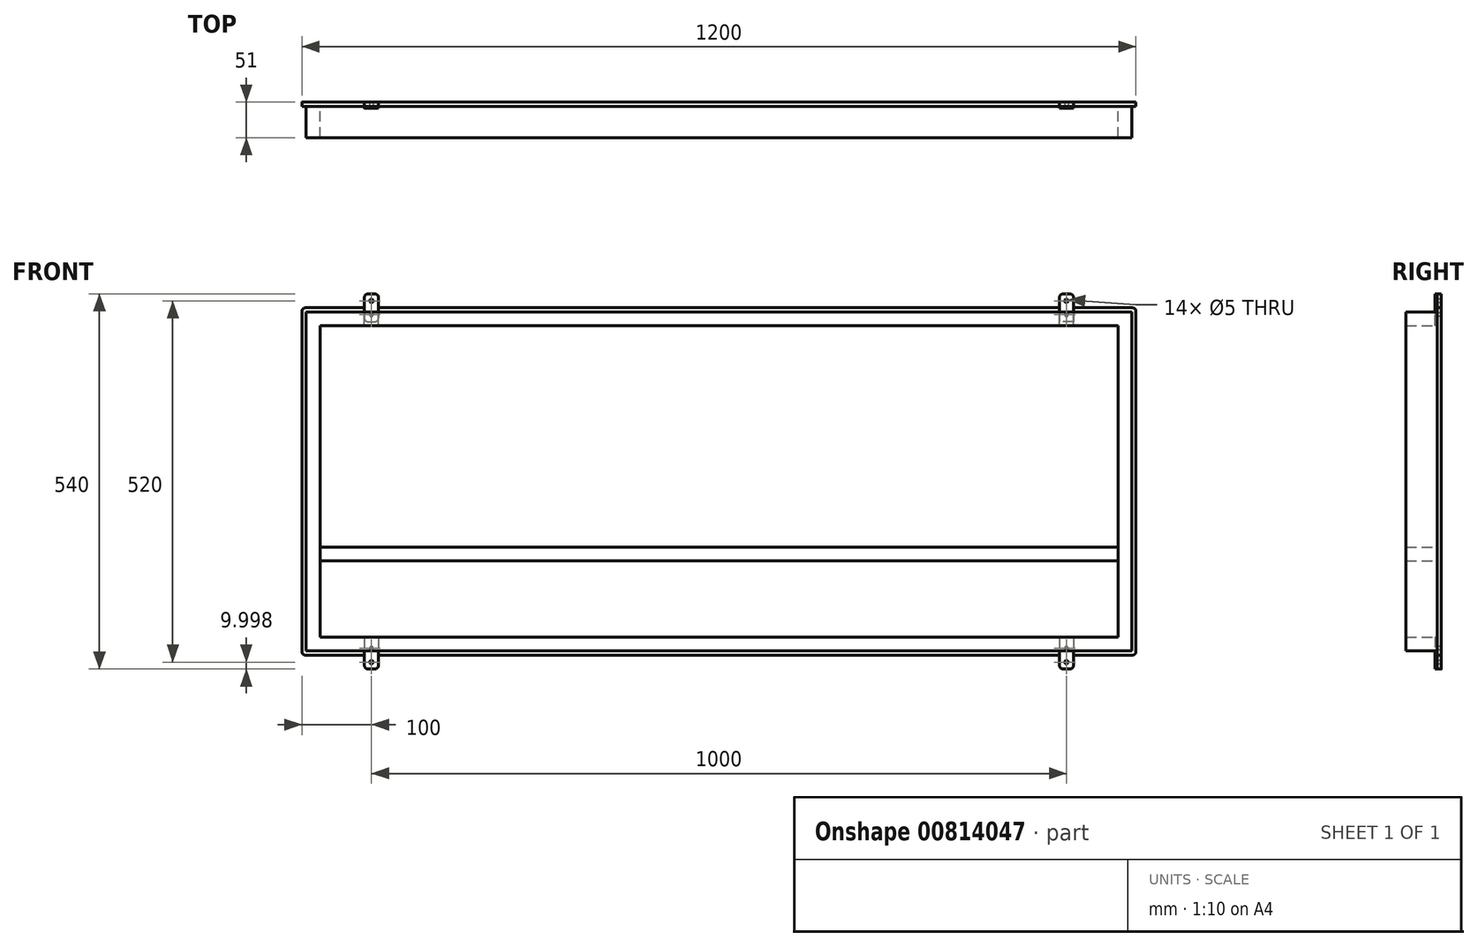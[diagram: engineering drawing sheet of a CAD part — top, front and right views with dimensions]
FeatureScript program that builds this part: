
annotation { "Feature Type Name" : "Feature", "Feature Type Description" : "" }
export const myFeature = defineFeature(function(context is Context, id is Id, definition is map)
    precondition{}
    {
        {
            var Q0;
            Q0=qCreatedBy(makeId("Front.planeOp"),FACE);
            var sketch = newSketch(context, id + "F0", { "sketchPlane" : qUnion([Q0])});
            skLineSegment(sketch, "E0.bottom", {"start": v(-594, 203.06) * mm, "end": v(594, 203.06) * mm});
            skLineSegment(sketch, "E0.top", {"start": v(-594, 223.06) * mm, "end": v(594, 223.06) * mm});
            skLineSegment(sketch, "E0.left", {"start": v(-594, 203.06) * mm, "end": v(-594, 223.06) * mm});
            skLineSegment(sketch, "E0.right", {"start": v(594, 203.06) * mm, "end": v(594, 223.06) * mm});
            skPoint(sketch, "E0.middle", {"position": v(0, 213.06) * mm});
            skLineSegment(sketch, "E1.bottom", {"start": v(-594, 203.06) * mm, "end": v(-574, 203.06) * mm});
            skLineSegment(sketch, "E1.top", {"start": v(-594, -244.94) * mm, "end": v(-574, -244.94) * mm});
            skLineSegment(sketch, "E1.left", {"start": v(-594, 203.06) * mm, "end": v(-594, -244.94) * mm});
            skLineSegment(sketch, "E1.right", {"start": v(-574, 203.06) * mm, "end": v(-574, -244.94) * mm});
            skLineSegment(sketch, "E2", {"start": v(-574, -20.94) * mm, "end": v(661.02, -20.94) * mm, "construction": true});
            skLineSegment(sketch, "E3", {"start": v(0, 203.06) * mm, "end": v(0, -288.66) * mm, "construction": true});
            skLineSegment(sketch, "E4.MirrorCS", {"start": v(594, -244.94) * mm, "end": v(574, -244.94) * mm});
            skLineSegment(sketch, "E5.MirrorCS", {"start": v(594, 203.06) * mm, "end": v(574, 203.06) * mm});
            skLineSegment(sketch, "E6.MirrorCS", {"start": v(594, 203.06) * mm, "end": v(594, -244.94) * mm});
            skLineSegment(sketch, "E7.MirrorCS", {"start": v(574, 203.06) * mm, "end": v(574, -244.94) * mm});
            skLineSegment(sketch, "E8.MirrorCS", {"start": v(-594, -244.94) * mm, "end": v(-594, -264.94) * mm});
            skLineSegment(sketch, "E9.MirrorCS", {"start": v(594, -244.94) * mm, "end": v(594, -264.94) * mm});
            skPoint(sketch, "E10.MirrorP", {"position": v(0, -254.94) * mm});
            skLineSegment(sketch, "E11.MirrorCS", {"start": v(-594, -244.94) * mm, "end": v(594, -244.94) * mm});
            skLineSegment(sketch, "E12.MirrorCS", {"start": v(-594, -264.94) * mm, "end": v(594, -264.94) * mm});
            skSolve(sketch);
        }
        {
            var Q0;
            Q0 = qSketchRegion(id + "F0", true);
            extrude(context, id + "F1", {"entities" : qUnion([Q0]), "depth" : 45 * mm, "offsetDistance" : 25 * mm});
        }
        {
            var Q0;
            Q0=makeQuery(id+"F1.opExtrude","CAP_FACE",FACE,{"disambiguationData":[OSD([sQuery(id+"F0.wireOp",EDGE,"E0.bottom"),sQuery(id+"F0.wireOp",EDGE,"E0.top"),sQuery(id+"F0.wireOp",EDGE,"E0.left"),sQuery(id+"F0.wireOp",EDGE,"E0.right"),sQuery(id+"F0.wireOp",EDGE,"E1.left"),sQuery(id+"F0.wireOp",EDGE,"E1.right"),sQuery(id+"F0.wireOp",EDGE,"E6.MirrorCS"),sQuery(id+"F0.wireOp",EDGE,"E7.MirrorCS"),sQuery(id+"F0.wireOp",EDGE,"E8.MirrorCS"),sQuery(id+"F0.wireOp",EDGE,"E9.MirrorCS"),sQuery(id+"F0.wireOp",EDGE,"E11.MirrorCS"),sQuery(id+"F0.wireOp",EDGE,"E12.MirrorCS")])],"isStart":true});
            var sketch = newSketch(context, id + "F2", { "sketchPlane" : qUnion([Q0])});
            skLineSegment(sketch, "E13.bottom", {"start": v(-600, 229.06) * mm, "end": v(600, 229.06) * mm});
            skLineSegment(sketch, "E13.top", {"start": v(-600, -270.94) * mm, "end": v(600, -270.94) * mm});
            skLineSegment(sketch, "E13.left", {"start": v(-600, 229.06) * mm, "end": v(-600, -270.94) * mm});
            skLineSegment(sketch, "E13.right", {"start": v(600, 229.06) * mm, "end": v(600, -270.94) * mm});
            skLineSegment(sketch, "E14.bottom", {"start": v(-510, 249.06) * mm, "end": v(-490, 249.06) * mm});
            skLineSegment(sketch, "E14.top", {"start": v(-510, 209.06) * mm, "end": v(-490, 209.06) * mm});
            skLineSegment(sketch, "E14.left", {"start": v(-510, 249.06) * mm, "end": v(-510, 209.06) * mm});
            skLineSegment(sketch, "E14.right", {"start": v(-490, 249.06) * mm, "end": v(-490, 209.06) * mm});
            skLineSegment(sketch, "E15", {"start": v(-500, 249.06) * mm, "end": v(-500, 209.06) * mm, "construction": true});
            skLineSegment(sketch, "E16", {"start": v(-513.73, 229.06) * mm, "end": v(-484.63, 229.06) * mm, "construction": true});
            skCircle(sketch, "E17", {"center": v(-500, 239.06) * mm, "radius": 2.5 * mm});
            skCircle(sketch, "E18.MirrorC", {"center": v(-500, 219.06) * mm, "radius": 2.5 * mm});
            skLineSegment(sketch, "E19", {"start": v(-574, -20.94) * mm, "end": v(615.98, -20.94) * mm, "construction": true});
            skLineSegment(sketch, "E20.MirrorCS", {"start": v(-510, -290.94) * mm, "end": v(-510, -250.94) * mm});
            skCircle(sketch, "E21.MirrorC", {"center": v(-500, -280.94) * mm, "radius": 2.5 * mm});
            skCircle(sketch, "E22.MirrorC", {"center": v(-500, -260.94) * mm, "radius": 2.5 * mm});
            skLineSegment(sketch, "E23.MirrorCS", {"start": v(-500, -290.94) * mm, "end": v(-500, -250.94) * mm, "construction": true});
            skLineSegment(sketch, "E24.MirrorCS", {"start": v(-510, -250.94) * mm, "end": v(-490, -250.94) * mm});
            skLineSegment(sketch, "E25.MirrorCS", {"start": v(-490, -290.94) * mm, "end": v(-490, -250.94) * mm});
            skLineSegment(sketch, "E26.MirrorCS", {"start": v(-513.73, -270.94) * mm, "end": v(-484.63, -270.94) * mm, "construction": true});
            skLineSegment(sketch, "E27.MirrorCS", {"start": v(-510, -290.94) * mm, "end": v(-490, -290.94) * mm});
            skLineSegment(sketch, "E28.MirrorCS", {"start": v(513.73, -270.94) * mm, "end": v(484.63, -270.94) * mm, "construction": true});
            skLineSegment(sketch, "E29.MirrorCS", {"start": v(510, 209.06) * mm, "end": v(490, 209.06) * mm});
            skCircle(sketch, "E30.MirrorC", {"center": v(500, -260.94) * mm, "radius": 2.5 * mm});
            skLineSegment(sketch, "E31.MirrorCS", {"start": v(490, 249.06) * mm, "end": v(490, 209.06) * mm});
            skLineSegment(sketch, "E32.MirrorCS", {"start": v(500, -290.94) * mm, "end": v(500, -250.94) * mm, "construction": true});
            skLineSegment(sketch, "E33.MirrorCS", {"start": v(510, -290.94) * mm, "end": v(510, -250.94) * mm});
            skCircle(sketch, "E34.MirrorC", {"center": v(500, 219.06) * mm, "radius": 2.5 * mm});
            skLineSegment(sketch, "E35.MirrorCS", {"start": v(513.73, 229.06) * mm, "end": v(484.63, 229.06) * mm, "construction": true});
            skLineSegment(sketch, "E36.MirrorCS", {"start": v(510, 249.06) * mm, "end": v(490, 249.06) * mm});
            skCircle(sketch, "E37.MirrorC", {"center": v(500, -280.94) * mm, "radius": 2.5 * mm});
            skLineSegment(sketch, "E38.MirrorCS", {"start": v(500, 249.06) * mm, "end": v(500, 209.06) * mm, "construction": true});
            skCircle(sketch, "E39.MirrorC", {"center": v(500, 239.06) * mm, "radius": 2.5 * mm});
            skLineSegment(sketch, "E40.MirrorCS", {"start": v(510, 249.06) * mm, "end": v(510, 209.06) * mm});
            skLineSegment(sketch, "E41.MirrorCS", {"start": v(490, -290.94) * mm, "end": v(490, -250.94) * mm});
            skLineSegment(sketch, "E42.MirrorCS", {"start": v(510, -250.94) * mm, "end": v(490, -250.94) * mm});
            skLineSegment(sketch, "E43.MirrorCS", {"start": v(510, -290.94) * mm, "end": v(490, -290.94) * mm});
            skSolve(sketch);
        }
        {
            var Q0;
            Q0 = qSketchRegion(id + "F2", true);
            extrude(context, id + "F3", {"entities" : qUnion([Q0]), "depth" : 6 * mm, "offsetDistance" : 25 * mm});
        }
        {
            var Q0;
            Q0=makeQuery(id+"F3.opExtrude","CAP_FACE",FACE,{"disambiguationData":[OSD([sQuery(id+"F2.wireOp",EDGE,"E13.bottom"),sQuery(id+"F2.wireOp",EDGE,"E13.top"),sQuery(id+"F2.wireOp",EDGE,"E13.left"),sQuery(id+"F2.wireOp",EDGE,"E13.right")])],"isStart":true});
            var sketch = newSketch(context, id + "F4", { "sketchPlane" : qUnion([Q0])});
            skLineSegment(sketch, "E44", {"start": v(-706.47, -135.32) * mm, "end": v(678.2, -135.32) * mm, "construction": true});
            skLineSegment(sketch, "E45.bottom", {"start": v(-574, -135.32) * mm, "end": v(574, -135.32) * mm});
            skLineSegment(sketch, "E45.top", {"start": v(-574, -115.32) * mm, "end": v(574, -115.32) * mm});
            skLineSegment(sketch, "E45.left", {"start": v(-574, -135.32) * mm, "end": v(-574, -115.32) * mm});
            skLineSegment(sketch, "E45.right", {"start": v(574, -135.32) * mm, "end": v(574, -115.32) * mm});
            skSolve(sketch);
        }
        {
            var Q0;
            Q0 = qSketchRegion(id + "F4", true);
            extrude(context, id + "F5", {"entities" : qUnion([Q0]), "depth" : 45 * mm, "offsetDistance" : 25 * mm});
        }
        {
            var Q0;
            Q0=makeQuery(id+"F3.opExtrude","SWEPT_EDGE",EDGE,{"disambiguationData":[OSD([sQuery(id+"F2.wireOp",EDGE,"E14.bottom"),sQuery(id+"F2.wireOp",EDGE,"E14.left")])]});
            var Q1;
            Q1=makeQuery(id+"F3.opExtrude","SWEPT_EDGE",EDGE,{"disambiguationData":[OSD([sQuery(id+"F2.wireOp",EDGE,"E14.bottom"),sQuery(id+"F2.wireOp",EDGE,"E14.right")])]});
            fillet(context, id + "F6", {"entities" : qUnion([Q0, Q1]), "radius" : 5 * mm, "tangentPropagation" : true, "allowEdgeOverflow" : false});
        }
        {
            var Q0;
            Q0=makeQuery(id+"FalYBE4lqMV1XQq_2.opExtrude","SWEPT_EDGE",EDGE,{"disambiguationData":[OSD([sQuery(id+"FmngfvzFBQgbU90_2.wireOp",EDGE,"03ac91fb-74bb-42a2-90a5-0a097265bc373.MirrorCS"),sQuery(id+"FmngfvzFBQgbU90_2.wireOp",EDGE,"03ac91fb-74bb-42a2-90a5-0a097265bc374.MirrorCS")])]});
            var Q1;
            Q1=makeQuery(id+"F3.opExtrude","SWEPT_EDGE",EDGE,{"disambiguationData":[OSD([sQuery(id+"F2.wireOp",EDGE,"E20.MirrorCS"),sQuery(id+"F2.wireOp",EDGE,"E27.MirrorCS")])]});
            var Q2;
            Q2=makeQuery(id+"F3.opExtrude","SWEPT_EDGE",EDGE,{"disambiguationData":[OSD([sQuery(id+"F2.wireOp",EDGE,"E25.MirrorCS"),sQuery(id+"F2.wireOp",EDGE,"E27.MirrorCS")])]});
            var Q3;
            Q3=makeQuery(id+"FalYBE4lqMV1XQq_2.opExtrude","SWEPT_EDGE",EDGE,{"disambiguationData":[OSD([sQuery(id+"FmngfvzFBQgbU90_2.wireOp",EDGE,"03ac91fb-74bb-42a2-90a5-0a097265bc373.MirrorCS"),sQuery(id+"FmngfvzFBQgbU90_2.wireOp",EDGE,"03ac91fb-74bb-42a2-90a5-0a097265bc377.MirrorCS")])]});
            var Q4;
            Q4=makeQuery(id+"F3.opExtrude","SWEPT_EDGE",EDGE,{"disambiguationData":[OSD([sQuery(id+"F2.wireOp",EDGE,"E36.MirrorCS"),sQuery(id+"F2.wireOp",EDGE,"E40.MirrorCS")])]});
            var Q5;
            Q5=makeQuery(id+"FalYBE4lqMV1XQq_2.opExtrude","SWEPT_EDGE",EDGE,{"disambiguationData":[OSD([sQuery(id+"FmngfvzFBQgbU90_2.wireOp",EDGE,"e4651637-c6b2-4f4a-9f87-8e23f2437c1f5.MirrorCS"),sQuery(id+"FmngfvzFBQgbU90_2.wireOp",EDGE,"e4651637-c6b2-4f4a-9f87-8e23f2437c1f9.MirrorCS")])]});
            var Q6;
            Q6=makeQuery(id+"F3.opExtrude","SWEPT_EDGE",EDGE,{"disambiguationData":[OSD([sQuery(id+"F2.wireOp",EDGE,"E31.MirrorCS"),sQuery(id+"F2.wireOp",EDGE,"E36.MirrorCS")])]});
            var Q7;
            Q7=makeQuery(id+"FalYBE4lqMV1XQq_2.opExtrude","SWEPT_EDGE",EDGE,{"disambiguationData":[OSD([sQuery(id+"FmngfvzFBQgbU90_2.wireOp",EDGE,"e4651637-c6b2-4f4a-9f87-8e23f2437c1f3.MirrorCS"),sQuery(id+"FmngfvzFBQgbU90_2.wireOp",EDGE,"e4651637-c6b2-4f4a-9f87-8e23f2437c1f6.MirrorCS")])]});
            var Q8;
            Q8=makeQuery(id+"FalYBE4lqMV1XQq_2.opExtrude","SWEPT_EDGE",EDGE,{"disambiguationData":[OSD([sQuery(id+"FmngfvzFBQgbU90_2.wireOp",EDGE,"e4651637-c6b2-4f4a-9f87-8e23f2437c1f5.MirrorCS"),sQuery(id+"FmngfvzFBQgbU90_2.wireOp",EDGE,"e4651637-c6b2-4f4a-9f87-8e23f2437c1f6.MirrorCS")])]});
            var Q9;
            Q9=makeQuery(id+"FalYBE4lqMV1XQq_2.opExtrude","SWEPT_EDGE",EDGE,{"disambiguationData":[OSD([sQuery(id+"FmngfvzFBQgbU90_2.wireOp",EDGE,"e4651637-c6b2-4f4a-9f87-8e23f2437c1f0.MirrorCS"),sQuery(id+"FmngfvzFBQgbU90_2.wireOp",EDGE,"e4651637-c6b2-4f4a-9f87-8e23f2437c1f15.MirrorCS")])]});
            var Q10;
            Q10=makeQuery(id+"F3.opExtrude","SWEPT_EDGE",EDGE,{"disambiguationData":[OSD([sQuery(id+"F2.wireOp",EDGE,"E33.MirrorCS"),sQuery(id+"F2.wireOp",EDGE,"E43.MirrorCS")])]});
            var Q11;
            Q11=makeQuery(id+"FalYBE4lqMV1XQq_2.opExtrude","SWEPT_EDGE",EDGE,{"disambiguationData":[OSD([sQuery(id+"FmngfvzFBQgbU90_2.wireOp",EDGE,"e4651637-c6b2-4f4a-9f87-8e23f2437c1f0.MirrorCS"),sQuery(id+"FmngfvzFBQgbU90_2.wireOp",EDGE,"e4651637-c6b2-4f4a-9f87-8e23f2437c1f8.MirrorCS")])]});
            var Q12;
            Q12=makeQuery(id+"F3.opExtrude","SWEPT_EDGE",EDGE,{"disambiguationData":[OSD([sQuery(id+"F2.wireOp",EDGE,"E41.MirrorCS"),sQuery(id+"F2.wireOp",EDGE,"E43.MirrorCS")])]});
            var Q13;
            Q13=makeQuery(id+"FalYBE4lqMV1XQq_2.opExtrude","SWEPT_EDGE",EDGE,{"disambiguationData":[OSD([sQuery(id+"FmngfvzFBQgbU90_2.wireOp",EDGE,"e4651637-c6b2-4f4a-9f87-8e23f2437c1f3.MirrorCS"),sQuery(id+"FmngfvzFBQgbU90_2.wireOp",EDGE,"e4651637-c6b2-4f4a-9f87-8e23f2437c1f9.MirrorCS")])]});
            fillet(context, id + "F7", {"entities" : qUnion([Q0, Q1, Q2, Q3, Q4, Q5, Q6, Q7, Q8, Q9, Q10, Q11, Q12, Q13]), "radius" : 5 * mm, "tangentPropagation" : true, "allowEdgeOverflow" : false});
        }
        {
            var Q0;
            Q0=makeQuery(id+"F1.opExtrude","SWEPT_FACE",FACE,{"disambiguationData":[OSD([sQuery(id+"F0.wireOp",EDGE,"E0.top")])]});
            var sketch = newSketch(context, id + "F8", { "sketchPlane" : qUnion([Q0])});
            skLineSegment(sketch, "E46.bottom", {"start": v(-510, 0) * mm, "end": v(-490, 0) * mm});
            skLineSegment(sketch, "E46.top", {"start": v(-510, -3) * mm, "end": v(-490, -3) * mm});
            skLineSegment(sketch, "E46.left", {"start": v(-510, 0) * mm, "end": v(-510, -3) * mm});
            skLineSegment(sketch, "E46.right", {"start": v(-490, 0) * mm, "end": v(-490, -3) * mm});
            skLineSegment(sketch, "E47.MirrorCS", {"start": v(490, 0) * mm, "end": v(490, -3) * mm});
            skLineSegment(sketch, "E48.MirrorCS", {"start": v(510, 0) * mm, "end": v(510, -3) * mm});
            skLineSegment(sketch, "E49.MirrorCS", {"start": v(510, -3) * mm, "end": v(490, -3) * mm});
            skLineSegment(sketch, "E50.MirrorCS", {"start": v(510, 0) * mm, "end": v(490, 0) * mm});
            skLineSegment(sketch, "E51.bottom", {"start": v(490, -3) * mm, "end": v(510, -3) * mm});
            skLineSegment(sketch, "E51.top", {"start": v(490, 0) * mm, "end": v(510, 0) * mm});
            skLineSegment(sketch, "E51.left", {"start": v(490, -3) * mm, "end": v(490, 0) * mm});
            skLineSegment(sketch, "E51.right", {"start": v(510, -3) * mm, "end": v(510, 0) * mm});
            skSolve(sketch);
        }
        {
            var Q0;
            Q0 = qSketchRegion(id + "F8", true);
            extrude(context, id + "F9", {"entities" : qUnion([Q0]), "operationType" : NewBodyOperationType.REMOVE, "oppositeDirection" : true, "depth" : 25 * mm, "offsetDistance" : 25 * mm});
        }
        {
            var Q0;
            Q0=makeQuery(id+"F3.opExtrude","CAP_FACE",FACE,{"disambiguationData":[OSD([sQuery(id+"F2.wireOp",EDGE,"E13.bottom"),sQuery(id+"F2.wireOp",EDGE,"E13.top"),sQuery(id+"F2.wireOp",EDGE,"E13.left"),sQuery(id+"F2.wireOp",EDGE,"E13.right"),sQuery(id+"F2.wireOp",EDGE,"E14.bottom"),sQuery(id+"F2.wireOp",EDGE,"E14.left"),sQuery(id+"F2.wireOp",EDGE,"E14.right"),sQuery(id+"F2.wireOp",EDGE,"E17"),sQuery(id+"F2.wireOp",EDGE,"E18.MirrorC"),sQuery(id+"F2.wireOp",EDGE,"E20.MirrorCS"),sQuery(id+"F2.wireOp",EDGE,"E21.MirrorC"),sQuery(id+"F2.wireOp",EDGE,"E22.MirrorC"),sQuery(id+"F2.wireOp",EDGE,"E25.MirrorCS"),sQuery(id+"F2.wireOp",EDGE,"E27.MirrorCS"),sQuery(id+"F2.wireOp",EDGE,"E30.MirrorC"),sQuery(id+"F2.wireOp",EDGE,"E31.MirrorCS"),sQuery(id+"F2.wireOp",EDGE,"E33.MirrorCS"),sQuery(id+"F2.wireOp",EDGE,"E34.MirrorC"),sQuery(id+"F2.wireOp",EDGE,"E36.MirrorCS"),sQuery(id+"F2.wireOp",EDGE,"E37.MirrorC"),sQuery(id+"F2.wireOp",EDGE,"E39.MirrorC"),sQuery(id+"F2.wireOp",EDGE,"E40.MirrorCS"),sQuery(id+"F2.wireOp",EDGE,"E41.MirrorCS"),sQuery(id+"F2.wireOp",EDGE,"E43.MirrorCS")])],"isStart":true});
            var sketch = newSketch(context, id + "F10", { "sketchPlane" : qUnion([Q0])});
            skLineSegment(sketch, "E52.bottom", {"start": v(-510, 249.06) * mm, "end": v(-490, 249.06) * mm});
            skLineSegment(sketch, "E52.top", {"start": v(-510, 209.06) * mm, "end": v(-490, 209.06) * mm});
            skLineSegment(sketch, "E52.left", {"start": v(-510, 249.06) * mm, "end": v(-510, 209.06) * mm});
            skLineSegment(sketch, "E52.right", {"start": v(-490, 249.06) * mm, "end": v(-490, 209.06) * mm});
            skCircle(sketch, "E53", {"center": v(-500, 239.06) * mm, "radius": 2.5 * mm});
            skCircle(sketch, "E54", {"center": v(-500, 219.06) * mm, "radius": 2.5 * mm});
            skLineSegment(sketch, "E55.MirrorCS", {"start": v(510, 249.06) * mm, "end": v(490, 249.06) * mm});
            skCircle(sketch, "E56.MirrorC", {"center": v(500, 239.06) * mm, "radius": 2.5 * mm});
            skLineSegment(sketch, "E57.MirrorCS", {"start": v(490, 249.06) * mm, "end": v(490, 209.06) * mm});
            skCircle(sketch, "E58.MirrorC", {"center": v(500, 219.06) * mm, "radius": 2.5 * mm});
            skLineSegment(sketch, "E59.MirrorCS", {"start": v(510, 209.06) * mm, "end": v(490, 209.06) * mm});
            skLineSegment(sketch, "E60.MirrorCS", {"start": v(510, 249.06) * mm, "end": v(510, 209.06) * mm});
            skLineSegment(sketch, "E61", {"start": v(-600, -20.94) * mm, "end": v(616.65, -20.94) * mm, "construction": true});
            skLineSegment(sketch, "E62.MirrorCS", {"start": v(-510, -250.94) * mm, "end": v(-490, -250.94) * mm});
            skLineSegment(sketch, "E63.MirrorCS", {"start": v(510, -290.94) * mm, "end": v(490, -290.94) * mm});
            skLineSegment(sketch, "E64.MirrorCS", {"start": v(-510, -290.94) * mm, "end": v(-510, -250.94) * mm});
            skLineSegment(sketch, "E65.MirrorCS", {"start": v(-510, -290.94) * mm, "end": v(-490, -290.94) * mm});
            skLineSegment(sketch, "E66.MirrorCS", {"start": v(510, -250.94) * mm, "end": v(490, -250.94) * mm});
            skCircle(sketch, "E67.MirrorC", {"center": v(500, -280.94) * mm, "radius": 2.5 * mm});
            skCircle(sketch, "E68.MirrorC", {"center": v(-500, -260.94) * mm, "radius": 2.5 * mm});
            skCircle(sketch, "E69.MirrorC", {"center": v(500, -260.94) * mm, "radius": 2.5 * mm});
            skLineSegment(sketch, "E70.MirrorCS", {"start": v(-490, -290.94) * mm, "end": v(-490, -250.94) * mm});
            skCircle(sketch, "E71.MirrorC", {"center": v(-500, -280.94) * mm, "radius": 2.5 * mm});
            skLineSegment(sketch, "E72.MirrorCS", {"start": v(490, -290.94) * mm, "end": v(490, -250.94) * mm});
            skLineSegment(sketch, "E73.MirrorCS", {"start": v(510, -290.94) * mm, "end": v(510, -250.94) * mm});
            skSolve(sketch);
        }
        {
            var Q0;
            Q0 = qSketchRegion(id + "F10", true);
            extrude(context, id + "F11", {"entities" : qUnion([Q0]), "depth" : 3 * mm, "offsetDistance" : 25 * mm});
        }
        {
            var Q0;
            Q0=makeQuery(id+"F11.opExtrude","SWEPT_EDGE",EDGE,{"disambiguationData":[OSD([sQuery(id+"F10.wireOp",EDGE,"E52.bottom"),sQuery(id+"F10.wireOp",EDGE,"E52.left")])]});
            var Q1;
            Q1=makeQuery(id+"F11.opExtrude","SWEPT_EDGE",EDGE,{"disambiguationData":[OSD([sQuery(id+"F10.wireOp",EDGE,"E52.bottom"),sQuery(id+"F10.wireOp",EDGE,"E52.right")])]});
            var Q2;
            Q2=makeQuery(id+"F11.opExtrude","SWEPT_EDGE",EDGE,{"disambiguationData":[OSD([sQuery(id+"F10.wireOp",EDGE,"E52.top"),sQuery(id+"F10.wireOp",EDGE,"E52.right")])]});
            var Q3;
            Q3=makeQuery(id+"F11.opExtrude","SWEPT_EDGE",EDGE,{"disambiguationData":[OSD([sQuery(id+"F10.wireOp",EDGE,"E52.top"),sQuery(id+"F10.wireOp",EDGE,"E52.left")])]});
            fillet(context, id + "F12", {"entities" : qUnion([Q0, Q1, Q2, Q3]), "radius" : 5 * mm, "tangentPropagation" : true, "allowEdgeOverflow" : false});
        }
        {
            var Q0;
            Q0=makeQuery(id+"F1.opExtrude","SWEPT_FACE",FACE,{"disambiguationData":[OSD([sQuery(id+"F0.wireOp",EDGE,"E12.MirrorCS")])]});
            var sketch = newSketch(context, id + "F13", { "sketchPlane" : qUnion([Q0])});
            skLineSegment(sketch, "E74.bottom", {"start": v(510, 0) * mm, "end": v(490, 0) * mm});
            skLineSegment(sketch, "E74.top", {"start": v(510, 3) * mm, "end": v(490, 3) * mm});
            skLineSegment(sketch, "E74.left", {"start": v(510, 0) * mm, "end": v(510, 3) * mm});
            skLineSegment(sketch, "E74.right", {"start": v(490, 0) * mm, "end": v(490, 3) * mm});
            skLineSegment(sketch, "E75.bottom", {"start": v(-510, 0) * mm, "end": v(-490, 0) * mm});
            skLineSegment(sketch, "E75.top", {"start": v(-510, 3) * mm, "end": v(-490, 3) * mm});
            skLineSegment(sketch, "E75.left", {"start": v(-510, 0) * mm, "end": v(-510, 3) * mm});
            skLineSegment(sketch, "E75.right", {"start": v(-490, 0) * mm, "end": v(-490, 3) * mm});
            skSolve(sketch);
        }
        {
            var Q0;
            Q0 = qSketchRegion(id + "F13", true);
            extrude(context, id + "F14", {"entities" : qUnion([Q0]), "operationType" : NewBodyOperationType.REMOVE, "oppositeDirection" : true, "depth" : 25 * mm, "offsetDistance" : 25 * mm});
        }
        {
            var Q0;
            Q0=makeQuery(id+"F11.opExtrude","SWEPT_EDGE",EDGE,{"disambiguationData":[OSD([sQuery(id+"F10.wireOp",EDGE,"E64.MirrorCS"),sQuery(id+"F10.wireOp",EDGE,"E65.MirrorCS")])]});
            var Q1;
            Q1=makeQuery(id+"F11.opExtrude","SWEPT_EDGE",EDGE,{"disambiguationData":[OSD([sQuery(id+"F10.wireOp",EDGE,"E65.MirrorCS"),sQuery(id+"F10.wireOp",EDGE,"E70.MirrorCS")])]});
            var Q2;
            Q2=makeQuery(id+"F11.opExtrude","SWEPT_EDGE",EDGE,{"disambiguationData":[OSD([sQuery(id+"F10.wireOp",EDGE,"E55.MirrorCS"),sQuery(id+"F10.wireOp",EDGE,"E60.MirrorCS")])]});
            var Q3;
            Q3=makeQuery(id+"F11.opExtrude","SWEPT_EDGE",EDGE,{"disambiguationData":[OSD([sQuery(id+"F10.wireOp",EDGE,"E55.MirrorCS"),sQuery(id+"F10.wireOp",EDGE,"E57.MirrorCS")])]});
            fillet(context, id + "F15", {"entities" : qUnion([Q0, Q1, Q2, Q3]), "radius" : 5 * mm, "tangentPropagation" : true, "allowEdgeOverflow" : false});
        }
        {
            var Q0;
            Q0=makeQuery(id+"F3.opExtrude","SWEPT_EDGE",EDGE,{"disambiguationData":[OSD([sQuery(id+"F2.wireOp",EDGE,"E13.bottom"),sQuery(id+"F2.wireOp",EDGE,"E13.left")])]});
            var Q1;
            Q1=makeQuery(id+"F11.opExtrude","SWEPT_EDGE",EDGE,{"disambiguationData":[OSD([sQuery(id+"F10.wireOp",EDGE,"E63.MirrorCS"),sQuery(id+"F10.wireOp",EDGE,"E73.MirrorCS")])]});
            var Q2;
            Q2=makeQuery(id+"F11.opExtrude","SWEPT_EDGE",EDGE,{"disambiguationData":[OSD([sQuery(id+"F10.wireOp",EDGE,"E63.MirrorCS"),sQuery(id+"F10.wireOp",EDGE,"E72.MirrorCS")])]});
            var Q3;
            Q3=makeQuery(id+"F3.opExtrude","SWEPT_EDGE",EDGE,{"disambiguationData":[OSD([sQuery(id+"F2.wireOp",EDGE,"E13.top"),sQuery(id+"F2.wireOp",EDGE,"E13.left")])]});
            var Q4;
            Q4=makeQuery(id+"F3.opExtrude","SWEPT_EDGE",EDGE,{"disambiguationData":[OSD([sQuery(id+"F2.wireOp",EDGE,"E13.top"),sQuery(id+"F2.wireOp",EDGE,"E13.right")])]});
            var Q5;
            Q5=makeQuery(id+"F3.opExtrude","SWEPT_EDGE",EDGE,{"disambiguationData":[OSD([sQuery(id+"F2.wireOp",EDGE,"E13.bottom"),sQuery(id+"F2.wireOp",EDGE,"E13.right")])]});
            fillet(context, id + "F16", {"entities" : qUnion([Q0, Q1, Q2, Q3, Q4, Q5]), "radius" : 5 * mm, "tangentPropagation" : true, "allowEdgeOverflow" : false});
        }
    });
